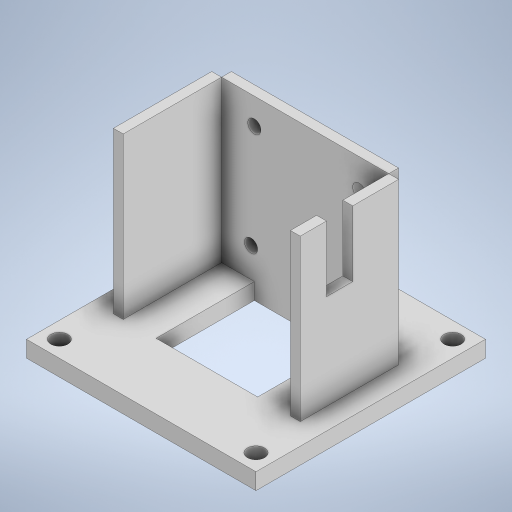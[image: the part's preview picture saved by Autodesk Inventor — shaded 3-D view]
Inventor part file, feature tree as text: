
AUTODESK INVENTOR PART (.ipt)
format: ipt  version: 2023 (Build 270158000, 158)  size: 337,920 bytes
history: native  units: mm
features: extrude x7, sketch x7, other x1
ambient origin geometry x8: Origin, YZ Plane, XZ Plane, XY Plane, X Axis, Y Axis, Z Axis, Center Point
bodies: Body1 (feature_tree)
feature tree (15):
  other  "Sólido1"
  extrude  "Extrusión1"  Depth=5.0mm TaperAngle=0.0deg
  extrude  "Extrusión4"  Depth=30.0mm
  extrude  "Extrusión5"  Depth=36.0mm
  extrude  "Extrusión6"  TaperAngle=0.0deg  [1 undecoded]
  extrude  "Extrusión7"  Depth=49.0mm
  extrude  "Extrusión10"  Depth=9.0mm
  extrude  "Extrusión11"  Depth=49.0mm TaperAngle=0.0deg
  sketch  "Boceto1"  dims[d2=10.0mm d7=5.0mm d8=0.0mm]
  sketch  "Boceto4"  dims[d21=51.0mm d22=30.0mm]
  sketch  "Boceto5"  dims[d23=57.0mm d24=36.0mm]
  sketch  "Boceto6"  dims[d25=5.0mm d26=0.0mm d27=0.0mm]
  sketch  "Boceto7"  dims[d28=49.0mm d29=0.0mm d30=4.0mm]
  sketch  "Boceto12"  dims[d31=9.0mm d32=9.0mm]
  sketch  "Boceto13"  dims[d33=40.0mm d35=360.0deg d37=49.0mm d38=0.0mm d39=49.0mm d40=0.0mm d63=70.0mm d64=70.0mm d65=60.0mm d66=5.2mm d67=5.2mm d68=5.2mm d69=5.2mm d70=5.0mm d71=0.0mm d72=8.0mm d73=20.0mm d74=8.0mm d75=10.0mm d76=0.0mm]
note: 1 required parameter value undecoded (feature->parameter linkage not recoverable at this tier; creation-order binding heuristic only, values carry confidence <= 0.55)
